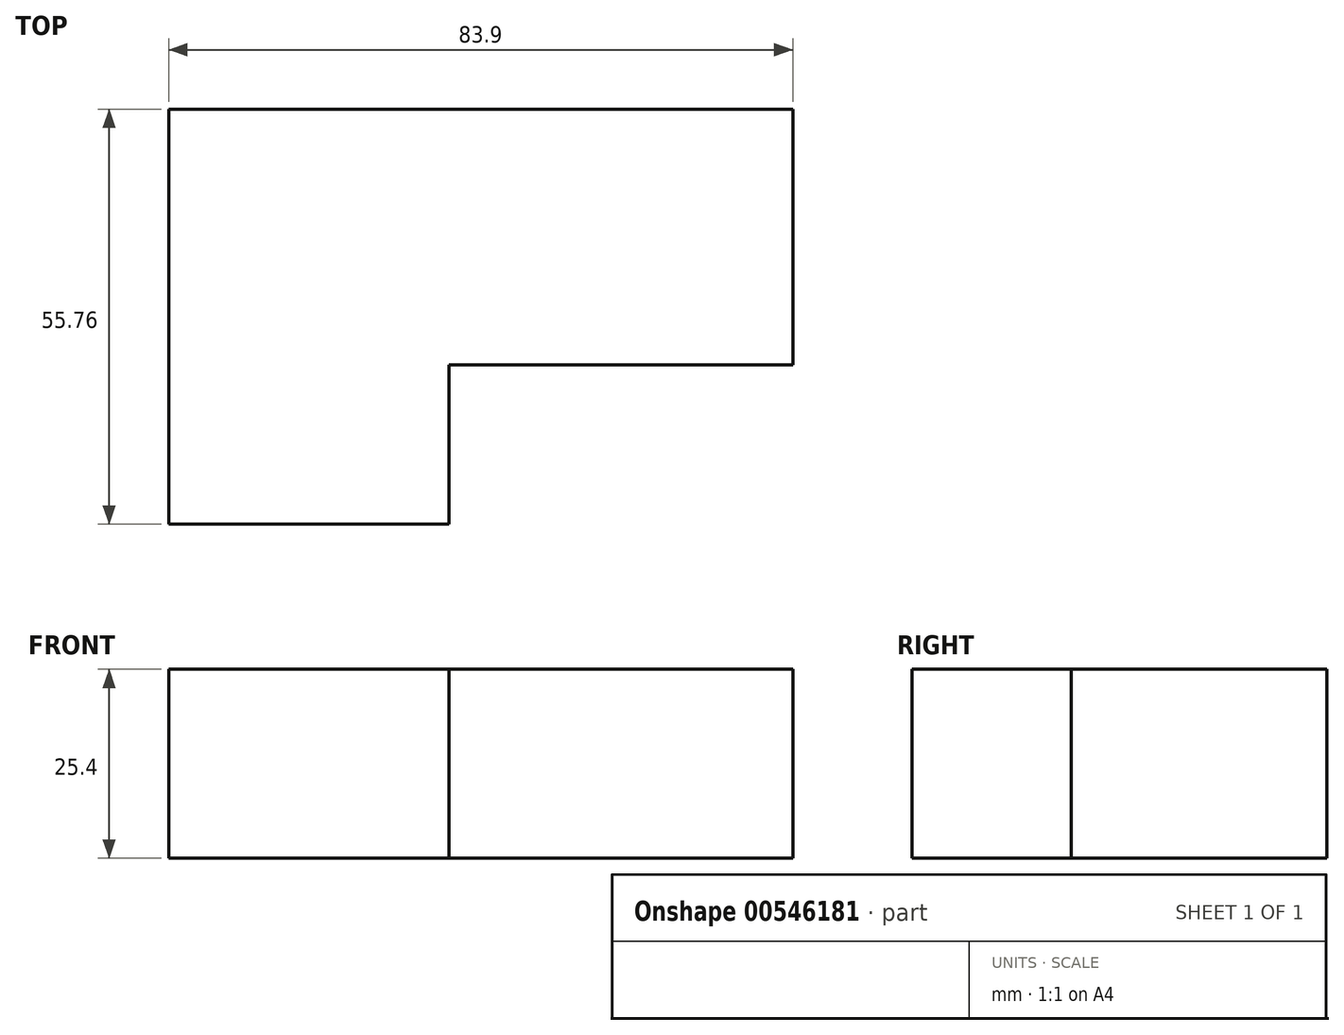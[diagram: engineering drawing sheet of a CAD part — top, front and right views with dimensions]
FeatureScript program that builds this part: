
annotation { "Feature Type Name" : "Feature", "Feature Type Description" : "" }
export const myFeature = defineFeature(function(context is Context, id is Id, definition is map)
    precondition{}
    {
        {
            var Q0;
            Q0=qCreatedBy(makeId("Top.planeOp"),FACE);
            var sketch = newSketch(context, id + "F0", { "sketchPlane" : qUnion([Q0])});
            skLineSegment(sketch, "E0", {"start": v(0, 0) * mm, "end": v(0, -44.84) * mm});
            skLineSegment(sketch, "E1", {"start": v(0, -44.84) * mm, "end": v(37.65, -44.84) * mm});
            skLineSegment(sketch, "E2", {"start": v(37.65, -44.84) * mm, "end": v(37.65, -23.43) * mm});
            skLineSegment(sketch, "E3", {"start": v(37.65, -23.43) * mm, "end": v(83.9, -23.43) * mm});
            skLineSegment(sketch, "E4", {"start": v(83.9, -23.43) * mm, "end": v(83.9, 10.92) * mm});
            skLineSegment(sketch, "E5", {"start": v(83.9, 10.92) * mm, "end": v(0, 10.92) * mm});
            skLineSegment(sketch, "E6", {"start": v(0, 10.92) * mm, "end": v(0, 0) * mm});
            skSolve(sketch);
        }
        {
            var Q0;
            Q0=makeQuery(id+"F0.imprint","IMPRINT",FACE,{"disambiguationData":[TD([[makeQuery(id+"F0.imprint","IMPRINT",EDGE,{"derivedFrom":sQuery(id+"F0.wireOp",EDGE,"E0")}),1.0]])]});
            extrude(context, id + "F1", {"entities" : qUnion([Q0]), "depth" : 25.4 * mm, "offsetDistance" : 25.4 * mm});
        }
    });
